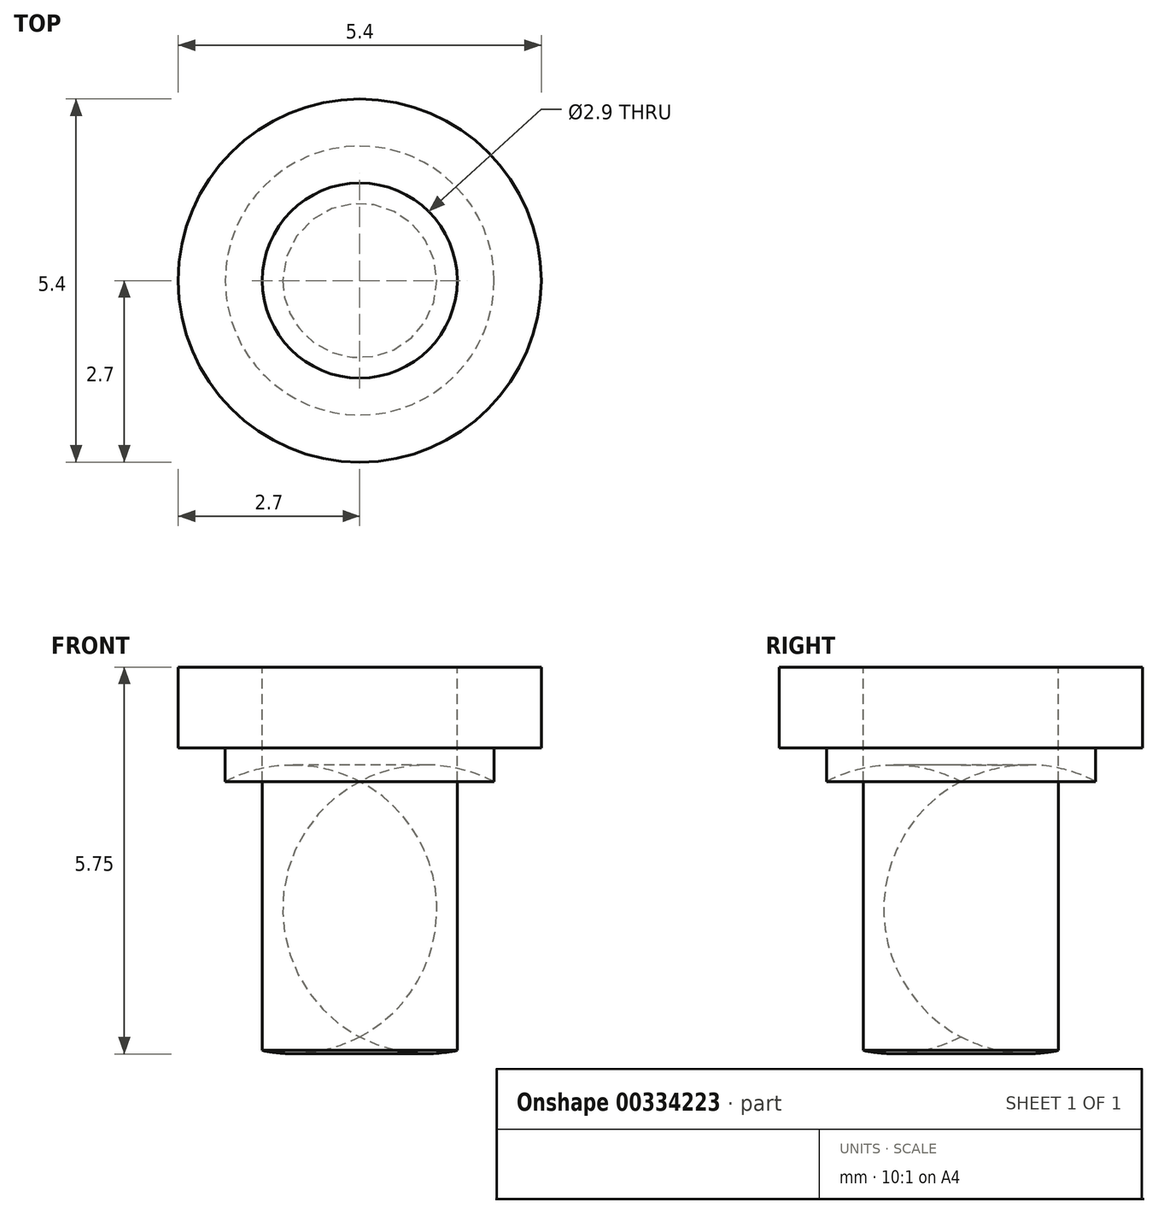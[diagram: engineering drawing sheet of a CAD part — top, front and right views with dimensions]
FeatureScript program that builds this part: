
annotation { "Feature Type Name" : "Feature", "Feature Type Description" : "" }
export const myFeature = defineFeature(function(context is Context, id is Id, definition is map)
    precondition{}
    {
        {
            var Q0;
            Q0=qCreatedBy(makeId("Front.planeOp"),FACE);
            var sketch = newSketch(context, id + "F0", { "sketchPlane" : qUnion([Q0])});
            skLineSegment(sketch, "E0", {"start": v(0, 10.7) * mm, "end": v(0, -12.69) * mm, "construction": true});
            skLineSegment(sketch, "E1", {"start": v(0, 5.16) * mm, "end": v(2.7, 5.16) * mm});
            skLineSegment(sketch, "E2", {"start": v(2.7, 5.16) * mm, "end": v(2.7, 3.96) * mm});
            skLineSegment(sketch, "E3", {"start": v(2.7, 3.96) * mm, "end": v(2, 3.96) * mm});
            skLineSegment(sketch, "E4", {"start": v(2, 3.96) * mm, "end": v(2, 3.46) * mm});
            skArc(sketch, "E5", {"start": v(0, -0.34) * mm, "mid": v(2.9, 0.56) * mm, "end": v(2, 3.46) * mm});
            skLineSegment(sketch, "E6", {"start": v(0, 5.16) * mm, "end": v(0, -0.34) * mm});
            skSolve(sketch);
        }
        {
            var Q0;
            Q0=makeQuery(id+"F0.imprint","IMPRINT",FACE,{"disambiguationData":[TD([[makeQuery(id+"F0.imprint","IMPRINT",EDGE,{"derivedFrom":sQuery(id+"F0.wireOp",EDGE,"E1")}),-1.0]])]});
            var Q1;
            Q1=sQuery(id+"F0.wireOp",EDGE,"E0");
            revolve(context, id + "F1", {"entities" : qUnion([Q0]), "axis" : qUnion([Q1]), "revolveType" : RevolveType.FULL});
        }
        {
            var Q0;
            Q0=makeQuery(id+"F1.opRevolve","SWEPT_FACE",FACE,{"disambiguationData":[OSD([sQuery(id+"F0.wireOp",EDGE,"E1")])]});
            var sketch = newSketch(context, id + "F2", { "sketchPlane" : qUnion([Q0])});
            skCircle(sketch, "E7", {"center": v(0, 0) * mm, "radius": 1.45 * mm});
            skSolve(sketch);
        }
        {
            var Q0;
            Q0 = qSketchRegion(id + "F2", true);
            extrude(context, id + "F3", {"entities" : qUnion([Q0]), "operationType" : NewBodyOperationType.REMOVE, "endBound" : BoundingType.THROUGH_ALL, "oppositeDirection" : true, "depth" : 25 * mm});
        }
    });
